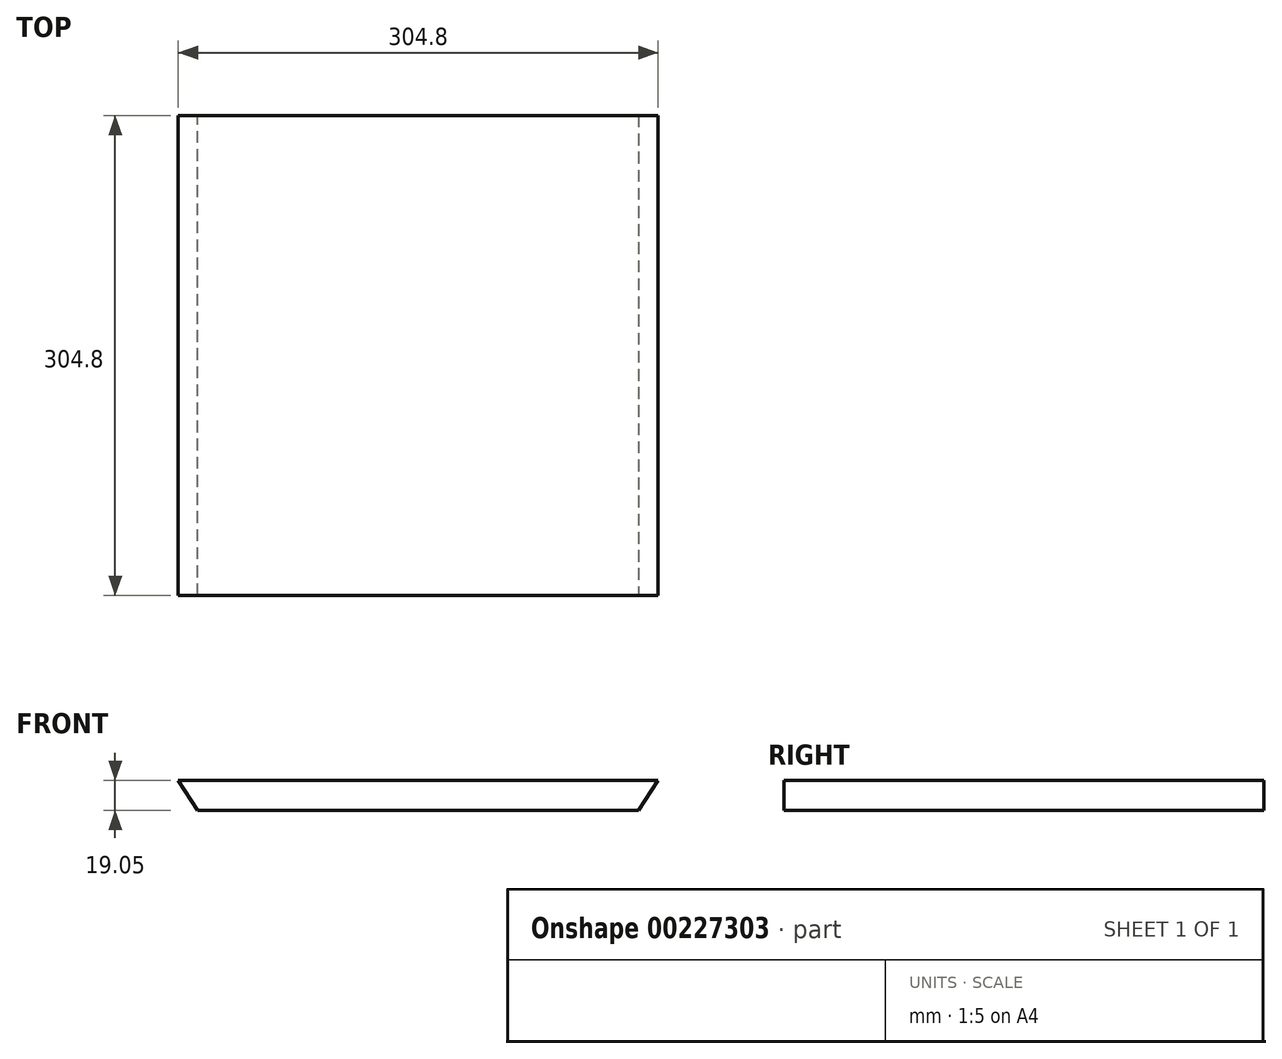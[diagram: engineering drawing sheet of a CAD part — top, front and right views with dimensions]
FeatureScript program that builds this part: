
annotation { "Feature Type Name" : "Feature", "Feature Type Description" : "" }
export const myFeature = defineFeature(function(context is Context, id is Id, definition is map)
    precondition{}
    {
        {
            var Q0;
            Q0=qCreatedBy(makeId("Top.planeOp"),FACE);
            var sketch = newSketch(context, id + "F0", { "sketchPlane" : qUnion([Q0])});
            skLineSegment(sketch, "E0.bottom", {"start": v(-148.98, 147.22) * mm, "end": v(155.82, 147.22) * mm});
            skLineSegment(sketch, "E0.top", {"start": v(-148.98, -157.58) * mm, "end": v(155.82, -157.58) * mm});
            skLineSegment(sketch, "E0.left", {"start": v(-148.98, 147.22) * mm, "end": v(-148.98, -157.58) * mm});
            skLineSegment(sketch, "E0.right", {"start": v(155.82, 147.22) * mm, "end": v(155.82, -157.58) * mm});
            skSolve(sketch);
        }
        {
            var Q0;
            Q0 = qSketchRegion(id + "F0", true);
            extrude(context, id + "F1", {"entities" : qUnion([Q0]), "depth" : 19.05 * mm});
        }
        {
            var Q0;
            Q0=makeQuery(id+"F1.opExtrude","CAP_EDGE",EDGE,{"disambiguationData":[OSD([sQuery(id+"F0.wireOp",EDGE,"E0.left")])],"isStart":true});
            var Q1;
            Q1=makeQuery(id+"F1.opExtrude","CAP_EDGE",EDGE,{"disambiguationData":[OSD([sQuery(id+"F0.wireOp",EDGE,"E0.right")])],"isStart":true});
            chamfer(context, id + "F2", {"entities" : qUnion([Q0, Q1]), "chamferType" : ChamferType.OFFSET_ANGLE, "width" : 19.05 * mm, "oppositeDirection" : false, "angle" : 33 * degree, "tangentPropagation" : true});
        }
    });
